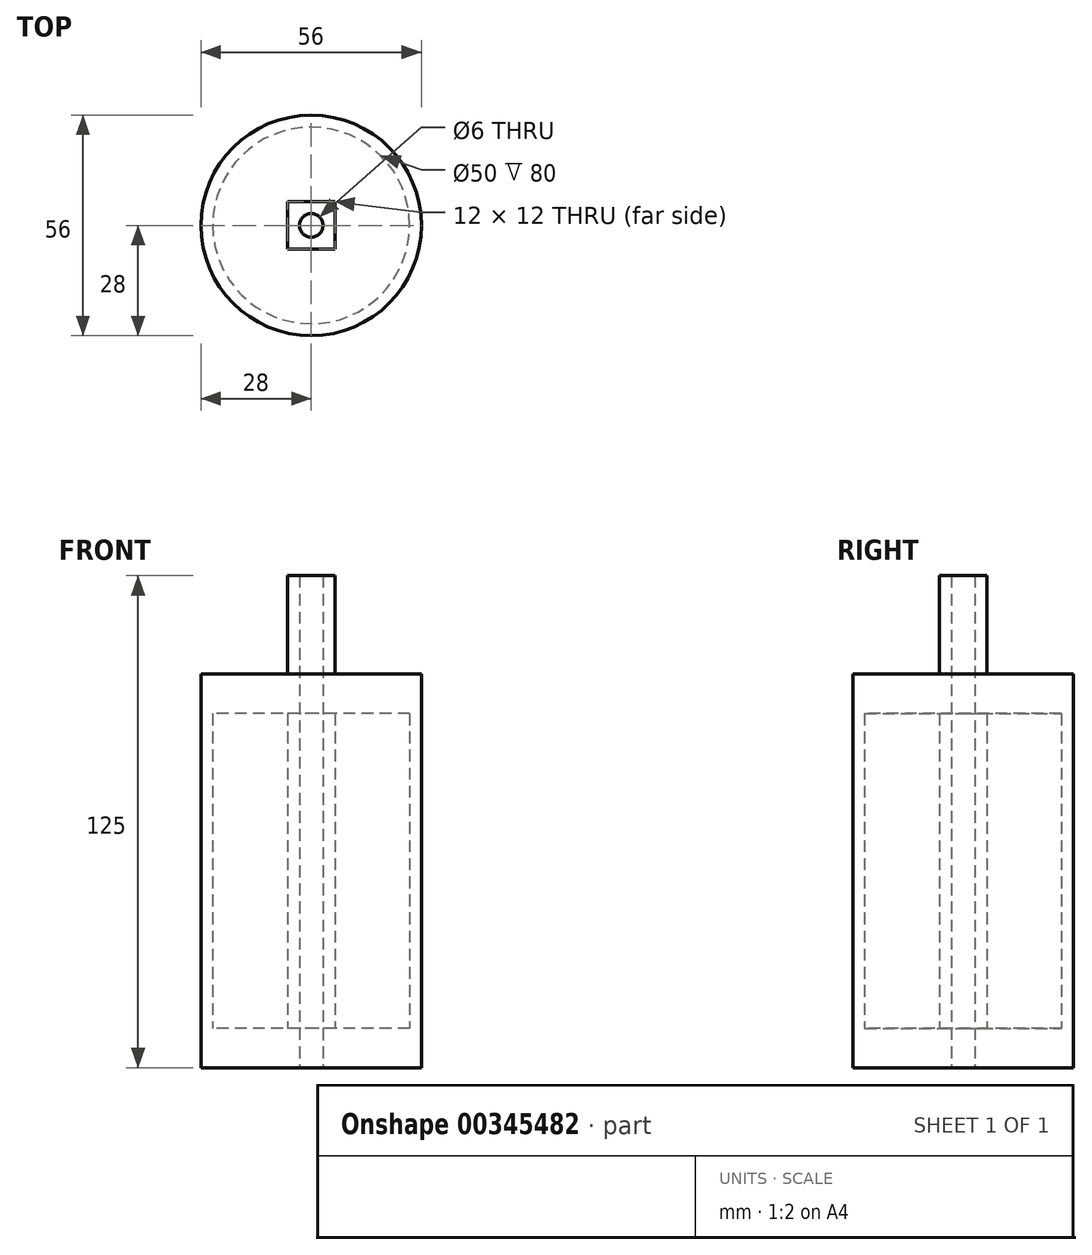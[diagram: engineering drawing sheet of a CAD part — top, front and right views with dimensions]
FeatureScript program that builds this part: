
annotation { "Feature Type Name" : "Feature", "Feature Type Description" : "" }
export const myFeature = defineFeature(function(context is Context, id is Id, definition is map)
    precondition{}
    {
        {
            var Q0;
            Q0=qCreatedBy(makeId("Top.planeOp"),FACE);
            var sketch = newSketch(context, id + "F0", { "sketchPlane" : qUnion([Q0])});
            skCircle(sketch, "E0", {"center": v(0, 0) * mm, "radius": 3 * mm});
            skLineSegment(sketch, "E1.bottom", {"start": v(6, -6) * mm, "end": v(-6, -6) * mm});
            skLineSegment(sketch, "E1.top", {"start": v(6, 6) * mm, "end": v(-6, 6) * mm});
            skLineSegment(sketch, "E1.left", {"start": v(6, -6) * mm, "end": v(6, 6) * mm});
            skLineSegment(sketch, "E1.right", {"start": v(-6, -6) * mm, "end": v(-6, 6) * mm});
            skCircle(sketch, "E2", {"center": v(0, 0) * mm, "radius": 28 * mm});
            skCircle(sketch, "E3", {"center": v(0, 0) * mm, "radius": 25 * mm});
            skSolve(sketch);
        }
        {
            var Q0;
            Q0=makeQuery(id+"F0.imprint","IMPRINT",FACE,{"disambiguationData":[TD([[makeQuery(id+"F0.imprint","IMPRINT",EDGE,{"derivedFrom":sQuery(id+"F0.wireOp",EDGE,"E2")}),1.0]])]});
            extrude(context, id + "F1", {"entities" : qUnion([Q0]), "depth" : 100 * mm});
        }
        {
            var Q0;
            Q0=makeQuery(id+"F0.imprint","IMPRINT",FACE,{"disambiguationData":[TD([[makeQuery(id+"F0.imprint","IMPRINT",EDGE,{"derivedFrom":sQuery(id+"F0.wireOp",EDGE,"E1.bottom")}),1.0]])]});
            extrude(context, id + "F2", {"entities" : qUnion([Q0]), "operationType" : NewBodyOperationType.ADD, "depth" : 10 * mm});
        }
        {
            var Q0;
            Q0=makeQuery(id+"F1.opExtrude","CAP_FACE",FACE,{"disambiguationData":[OSD([sQuery(id+"F0.wireOp",EDGE,"E2"),sQuery(id+"F0.wireOp",EDGE,"E3")])],"isStart":false});
            var sketch = newSketch(context, id + "F3", { "sketchPlane" : qUnion([Q0])});
            skCircle(sketch, "E4.0", {"center": v(0, 0) * mm, "radius": 25 * mm});
            skLineSegment(sketch, "E5.0", {"start": v(6, 6) * mm, "end": v(-6, 6) * mm});
            skLineSegment(sketch, "E6.0", {"start": v(-6, -6) * mm, "end": v(-6, 6) * mm});
            skLineSegment(sketch, "E7.0", {"start": v(6, -6) * mm, "end": v(-6, -6) * mm});
            skLineSegment(sketch, "E8.0", {"start": v(6, -6) * mm, "end": v(6, 6) * mm});
            skSolve(sketch);
        }
        {
            var Q0;
            Q0=makeQuery(id+"F3.imprint","IMPRINT",FACE,{"disambiguationData":[TD([[makeQuery(id+"F3.imprint","IMPRINT",EDGE,{"derivedFrom":sQuery(id+"F3.wireOp",EDGE,"E4.0")}),1.0]])]});
            extrude(context, id + "F4", {"entities" : qUnion([Q0]), "operationType" : NewBodyOperationType.ADD, "oppositeDirection" : true, "depth" : 10 * mm});
        }
        {
            var Q0;
            Q0=makeQuery(id+"F0.imprint","IMPRINT",FACE,{"disambiguationData":[TD([[makeQuery(id+"F0.imprint","IMPRINT",EDGE,{"derivedFrom":sQuery(id+"F0.wireOp",EDGE,"E0")}),-1.0]])]});
            extrude(context, id + "F5", {"entities" : qUnion([Q0]), "depth" : 10 * mm});
        }
        {
            var Q0;
            Q0=makeQuery(id+"F0.imprint","IMPRINT",FACE,{"disambiguationData":[TD([[makeQuery(id+"F0.imprint","IMPRINT",EDGE,{"derivedFrom":sQuery(id+"F0.wireOp",EDGE,"E0")}),-1.0]])]});
            extrude(context, id + "F6", {"entities" : qUnion([Q0]), "operationType" : NewBodyOperationType.ADD, "depth" : 125 * mm});
        }
    });
